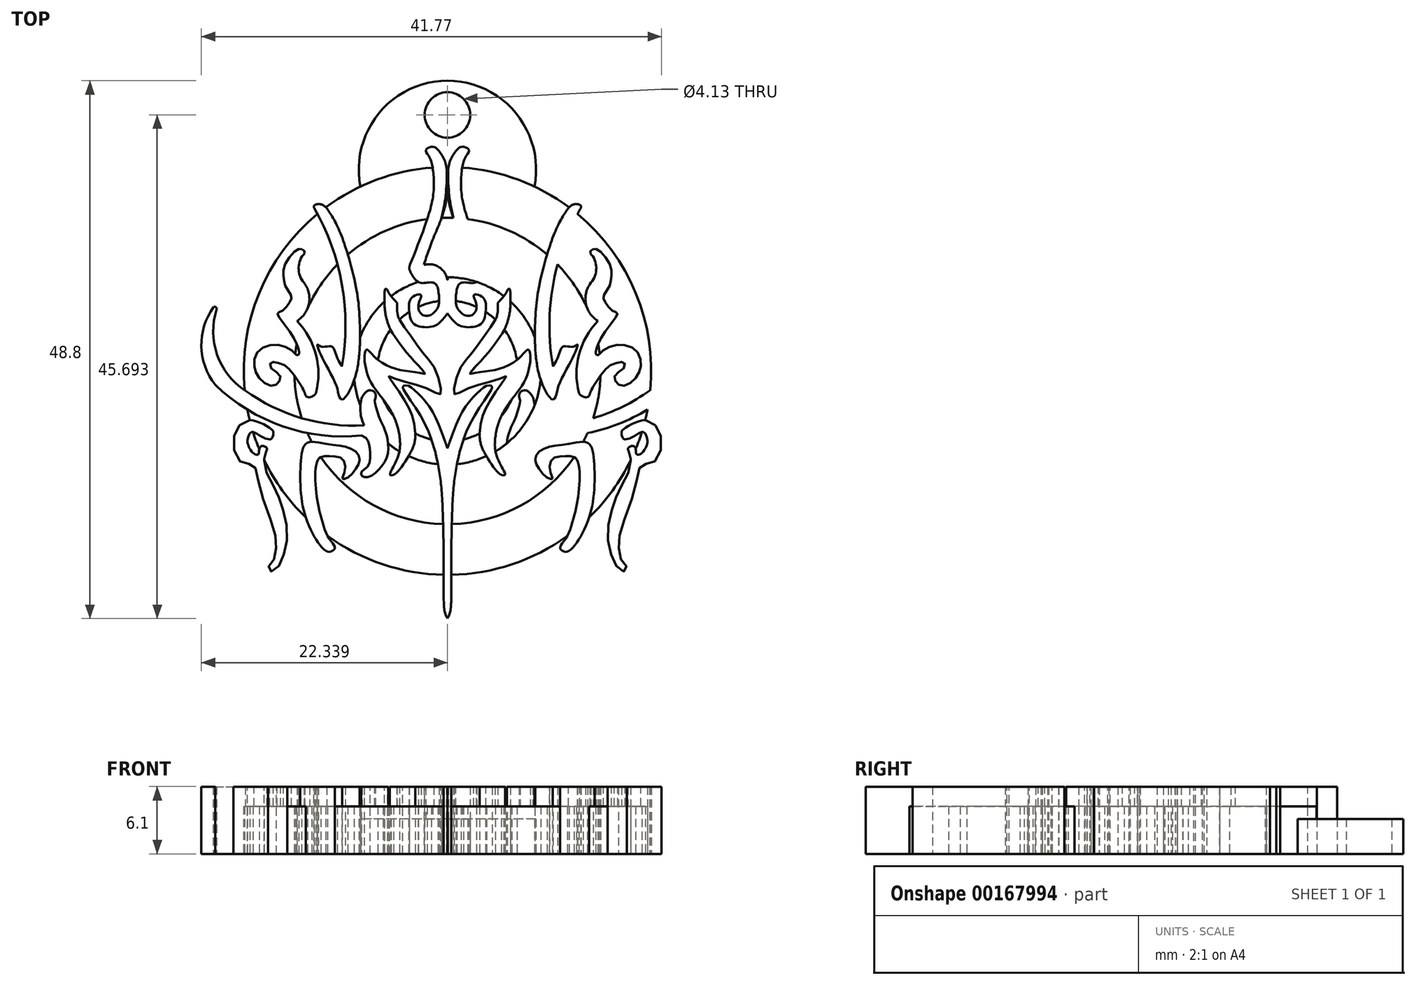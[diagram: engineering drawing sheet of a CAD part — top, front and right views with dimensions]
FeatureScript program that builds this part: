
annotation { "Feature Type Name" : "Feature", "Feature Type Description" : "" }
export const myFeature = defineFeature(function(context is Context, id is Id, definition is map)
    precondition{}
    {
        {
            var Q0;
            Q0=qCreatedBy(makeId("Top.planeOp"),FACE);
            var sketch = newSketch(context, id + "F0", { "sketchPlane" : qUnion([Q0])});
            skFitSpline(sketch, "E0", {"points": [v(-0.36, 46.17) * mm, v(-0.6, 47.55) * mm, v(-1.23, 48.6) * mm, v(-1.62, 48.85) * mm, v(-2.1, 48.77) * mm, v(-2.32, 48.53) * mm, v(-2.06, 48.04) * mm, v(-1.74, 47.2) * mm, v(-1.6, 45.2) * mm, v(-2.2, 42.32) * mm, v(-3.77, 38.15) * mm, v(-3.8, 37.74) * mm, v(-3.02, 36.6) * mm, v(-2.13, 36.55) * mm, v(-1.45, 36.42) * mm, v(-1.17, 35.66) * mm, v(-1.17, 34.49) * mm, v(-1.6, 33.8) * mm, v(-2.13, 33.53) * mm, v(-2.72, 33.68) * mm, v(-3, 34.46) * mm, v(-2.77, 35.23) * mm, v(-2.8, 35.44) * mm, v(-3.57, 35.2) * mm, v(-3.85, 34.31) * mm, v(-3.64, 33.08) * mm, v(-3.09, 32.61) * mm, v(-2.07, 32.5) * mm, v(-1.21, 32.8) * mm, v(-0.36, 33.76) * mm], "startDerivative": vector(-2.43, 33.8) * mm, "endDerivative": vector(19.13, 26.66) * mm});
            skFitSpline(sketch, "E1", {"points": [v(-5.8, 35.84) * mm, v(-5.55, 35.4) * mm, v(-4.93, 34.7) * mm], "startDerivative": vector(0.49, -1.03) * mm, "endDerivative": vector(1.22, -1.28) * mm});
            skFitSpline(sketch, "E2", {"points": [v(-4.93, 34.7) * mm, v(-4.93, 34.14) * mm, v(-4.8, 33.35) * mm, v(-3.77, 31.8) * mm, v(-2.5, 30.04) * mm, v(-1.41, 28.52) * mm, v(-0.96, 26.51) * mm, v(-1.06, 26.41) * mm, v(-2.38, 27) * mm, v(-4.76, 27.69) * mm, v(-5.7, 28.02) * mm, v(-5.58, 27.82) * mm, v(-4.93, 26.92) * mm, v(-3.9, 25.26) * mm, v(-3.45, 24) * mm, v(-3.34, 22.1) * mm, v(-4.21, 20.3) * mm, v(-5.14, 19.16) * mm, v(-5.57, 19.1) * mm, v(-5.44, 19.54) * mm, v(-4.93, 20.51) * mm, v(-4.67, 21.65) * mm, v(-4.93, 23.59) * mm, v(-5.92, 25.58) * mm, v(-7.26, 27.41) * mm, v(-7.83, 29.07) * mm, v(-7.86, 30.2) * mm, v(-7.68, 30.46) * mm, v(-7.41, 30.27) * mm, v(-6.76, 29.59) * mm, v(-5.54, 28.88) * mm, v(-4.11, 28.52) * mm, v(-2.73, 28.32) * mm, v(-2.41, 28.26) * mm, v(-2.68, 28.66) * mm, v(-3.96, 30.06) * mm, v(-4.93, 31.35) * mm, v(-5.5, 32.22) * mm, v(-5.98, 33.65) * mm, v(-6.08, 35.05) * mm, v(-5.98, 35.98) * mm, v(-5.8, 35.84) * mm], "startDerivative": vector(-0.34, -32.03) * mm, "endDerivative": vector(17.35, -24.3) * mm});
            skFitSpline(sketch, "E3", {"points": [v(-0.36, 6.06) * mm, v(-0.6, 6.68) * mm, v(-0.7, 9.02) * mm, v(-0.82, 16.57) * mm, v(-1.2, 19.94) * mm, v(-2.54, 23.98) * mm, v(-4.4, 26.99) * mm, v(-4.35, 27.17) * mm, v(-3.98, 27.2) * mm, v(-3.18, 26.63) * mm, v(-1.8, 24.94) * mm, v(-0.65, 22.32) * mm, v(-0.36, 21.5) * mm], "startDerivative": vector(-5.82, 11.46) * mm, "endDerivative": vector(4.22, -12.55) * mm});
            skLineSegment(sketch, "E4", {"start": v(-0.36, 46.17) * mm, "end": v(-0.36, 46.17) * mm});
            skFitSpline(sketch, "E5", {"points": [v(-2.5, 38.16) * mm, v(-1.58, 38.16) * mm, v(-0.68, 37.53) * mm, v(-0.36, 36.78) * mm], "startDerivative": vector(2.77, 0.4) * mm, "endDerivative": vector(0.67, -2.46) * mm});
            skArc(sketch, "E6", {"start": v(-9.94, 28.94) * mm, "mid": v(-9.94, 36.35) * mm, "end": v(-12.47, 43.31) * mm});
            skFitSpline(sketch, "E7", {"points": [v(-12.47, 43.31) * mm, v(-12.47, 43.53) * mm, v(-11.92, 43.67) * mm, v(-11.33, 43.31) * mm], "startDerivative": vector(-0.3, 1) * mm, "endDerivative": vector(1.33, -1.17) * mm});
            skFitSpline(sketch, "E8", {"points": [v(-11.33, 43.31) * mm, v(-10.2, 41.31) * mm, v(-8.7, 36.35) * mm, v(-8.33, 32.98) * mm, v(-8.7, 28.1) * mm, v(-9.9, 25.95) * mm, v(-10.17, 26.15) * mm, v(-10.43, 27.14) * mm, v(-11.67, 29.6) * mm, v(-12.15, 30.73) * mm], "startDerivative": vector(10.19, -15.18) * mm, "endDerivative": vector(-4.43, 12.34) * mm});
            skFitSpline(sketch, "E9", {"points": [v(-12.15, 30.73) * mm, v(-12.15, 30.92) * mm, v(-11.84, 30.73) * mm, v(-10.86, 30.73) * mm, v(-10.49, 30.02) * mm, v(-9.94, 28.94) * mm], "startDerivative": vector(-0.34, 2.51) * mm, "endDerivative": vector(2.32, -3.87) * mm});
            skArc(sketch, "E10", {"start": v(-13.32, 39.21) * mm, "mid": v(-13.87, 37.88) * mm, "end": v(-13.39, 36.53) * mm});
            skArc(sketch, "E11", {"start": v(-14.03, 33.06) * mm, "mid": v(-12.92, 34.65) * mm, "end": v(-13.39, 36.53) * mm});
            skArc(sketch, "E12", {"start": v(-12.3, 26.5) * mm, "mid": v(-12.3, 30.01) * mm, "end": v(-14.03, 33.06) * mm});
            skFitSpline(sketch, "E13", {"points": [v(-12.3, 26.5) * mm, v(-12.63, 26.2) * mm, v(-13.12, 26.17) * mm, v(-13.36, 26.62) * mm, v(-14.5, 28.46) * mm, v(-15.23, 29.07) * mm, v(-16.06, 29.33) * mm, v(-16.42, 29.26) * mm, v(-16.42, 28.83) * mm, v(-15.64, 28.23) * mm, v(-15.55, 27.76) * mm, v(-15.94, 27.25) * mm, v(-16.7, 27.29) * mm, v(-17.61, 28.1) * mm, v(-17.9, 29) * mm, v(-17.7, 30.12) * mm, v(-16.63, 30.84) * mm, v(-15.17, 30.74) * mm, v(-14.29, 30.2) * mm, v(-14.08, 29.98) * mm, v(-13.85, 30.04) * mm, v(-13.93, 30.63) * mm, v(-14.63, 32.05) * mm, v(-15.8, 33.66) * mm, v(-15.76, 33.82) * mm, v(-15.21, 34.08) * mm, v(-14.61, 34.92) * mm, v(-14.53, 35.34) * mm, v(-15.03, 36.16) * mm, v(-15.23, 37.03) * mm, v(-15.11, 38.16) * mm, v(-14, 39.52) * mm, v(-13.6, 39.58) * mm, v(-13.36, 39.42) * mm, v(-13.32, 39.21) * mm], "startDerivative": vector(-12.43, -15.12) * mm, "endDerivative": vector(-0.18, -14.31) * mm});
            skArc(sketch, "E14", {"start": v(-21.59, 34.32) * mm, "mid": v(-22.7, 30.77) * mm, "end": v(-21.44, 27.27) * mm});
            skArc(sketch, "E15", {"start": v(-21.44, 27.27) * mm, "mid": v(-15.31, 23.5) * mm, "end": v(-8.16, 22.66) * mm});
            skArc(sketch, "E16", {"start": v(-21.3, 34.14) * mm, "mid": v(-21.4, 34.31) * mm, "end": v(-21.59, 34.32) * mm});
            skArc(sketch, "E17", {"start": v(-21.3, 34.14) * mm, "mid": v(-21.27, 30) * mm, "end": v(-18.72, 26.75) * mm});
            skArc(sketch, "E18", {"start": v(-18.72, 26.75) * mm, "mid": v(-13.59, 24.24) * mm, "end": v(-7.91, 23.58) * mm});
            skArc(sketch, "E19", {"start": v(-8.12, 26.15) * mm, "mid": v(-8.27, 24.85) * mm, "end": v(-7.91, 23.58) * mm});
            skFitSpline(sketch, "E20", {"points": [v(-8.12, 26.15) * mm, v(-7.77, 26.6) * mm, v(-7.34, 26.77) * mm, v(-6.94, 26.55) * mm, v(-6.88, 26.15) * mm, v(-6.96, 25.77) * mm, v(-6.45, 24.08) * mm, v(-6, 23.07) * mm, v(-5.75, 21.97) * mm, v(-5.85, 20.7) * mm, v(-6.4, 19.81) * mm, v(-7.38, 18.96) * mm, v(-7.97, 18.92) * mm, v(-8.19, 19.12) * mm, v(-8.12, 19.43) * mm, v(-7.57, 19.93) * mm, v(-7.37, 21.18) * mm, v(-7.52, 22.02) * mm, v(-8.16, 22.66) * mm], "startDerivative": vector(6.68, 10.52) * mm, "endDerivative": vector(-21.28, 6.18) * mm});
            skFitSpline(sketch, "E21", {"points": [v(-16.63, 10.72) * mm, v(-16.2, 11.28) * mm, v(-15.9, 12.49) * mm, v(-16.14, 14.2) * mm, v(-17.43, 18.06) * mm, v(-17.86, 19.8) * mm, v(-18.4, 20.1) * mm, v(-19.17, 20.3) * mm, v(-19.8, 21.82) * mm, v(-19.39, 23.4) * mm, v(-18.32, 24.07) * mm, v(-16.41, 23.3) * mm, v(-16.17, 22.95) * mm, v(-16.3, 22.4) * mm, v(-16.63, 22.33) * mm, v(-17.48, 22.7) * mm, v(-18.16, 22.97) * mm, v(-18.5, 22.36) * mm, v(-18.4, 21.66) * mm, v(-17.94, 21.02) * mm, v(-17.54, 20.96) * mm, v(-17.4, 21.58) * mm, v(-17.08, 21.71) * mm, v(-16.76, 21.52) * mm, v(-16.92, 20.9) * mm, v(-16.84, 19.46) * mm, v(-15.98, 17.74) * mm, v(-15.4, 16.21) * mm, v(-14.91, 13.99) * mm, v(-15.2, 11.9) * mm, v(-15.88, 10.6) * mm, v(-16.5, 10.34) * mm, v(-16.63, 10.72) * mm]});
            skFitSpline(sketch, "E22", {"points": [v(-13.09, 22) * mm, v(-13.68, 20.21) * mm, v(-13.44, 16) * mm, v(-12.26, 13.18) * mm, v(-11.29, 12.14) * mm, v(-10.78, 12.22) * mm, v(-10.6, 12.54) * mm, v(-11.13, 13.37) * mm, v(-11.9, 15.54) * mm, v(-12.34, 18.1) * mm, v(-12.15, 20.43) * mm, v(-11.67, 20.77) * mm, v(-10.91, 20.77) * mm, v(-9.87, 20.53) * mm, v(-9.7, 19.38) * mm, v(-9.9, 18.74) * mm, v(-9.33, 18.9) * mm, v(-8.55, 19.84) * mm, v(-8.34, 20.61) * mm, v(-8.74, 21.26) * mm, v(-9.87, 21.71) * mm, v(-11.4, 21.9) * mm, v(-13.09, 22) * mm]});
            skFitSpline(sketch, "E23.MirrorCS", {"points": [v(-0.36, 6.06) * mm, v(-0.12, 6.68) * mm, v(-0.02, 9.02) * mm, v(0.1, 16.57) * mm, v(0.48, 19.94) * mm, v(1.82, 23.98) * mm, v(3.68, 26.99) * mm, v(3.63, 27.17) * mm, v(3.26, 27.2) * mm, v(2.46, 26.63) * mm, v(1.07, 24.94) * mm, v(-0.08, 22.32) * mm, v(-0.36, 21.5) * mm], "startDerivative": vector(5.82, 11.46) * mm, "endDerivative": vector(-4.22, -12.55) * mm});
            skFitSpline(sketch, "E24.MirrorCS", {"points": [v(1.78, 38.16) * mm, v(0.86, 38.16) * mm, v(-0.05, 37.53) * mm, v(-0.36, 36.78) * mm], "startDerivative": vector(-2.77, 0.4) * mm, "endDerivative": vector(-0.67, -2.46) * mm});
            skFitSpline(sketch, "E25.MirrorCS", {"points": [v(-0.36, 46.17) * mm, v(-0.13, 47.55) * mm, v(0.51, 48.6) * mm, v(0.9, 48.85) * mm, v(1.38, 48.77) * mm, v(1.6, 48.53) * mm, v(1.34, 48.04) * mm, v(1.02, 47.2) * mm, v(0.87, 45.2) * mm, v(1.47, 42.32) * mm, v(3.04, 38.15) * mm, v(3.09, 37.74) * mm, v(2.3, 36.6) * mm, v(1.4, 36.55) * mm, v(0.72, 36.42) * mm, v(0.45, 35.66) * mm, v(0.45, 34.49) * mm, v(0.87, 33.8) * mm, v(1.4, 33.53) * mm, v(2, 33.68) * mm, v(2.28, 34.46) * mm, v(2.04, 35.23) * mm, v(2.09, 35.44) * mm, v(2.85, 35.2) * mm, v(3.13, 34.31) * mm, v(2.92, 33.08) * mm, v(2.37, 32.61) * mm, v(1.35, 32.5) * mm, v(0.5, 32.8) * mm, v(-0.36, 33.76) * mm], "startDerivative": vector(2.43, 33.8) * mm, "endDerivative": vector(-19.13, 26.66) * mm});
            skFitSpline(sketch, "E26.MirrorCS", {"points": [v(5.08, 35.84) * mm, v(4.83, 35.4) * mm, v(4.21, 34.7) * mm], "startDerivative": vector(-0.49, -1.03) * mm, "endDerivative": vector(-1.22, -1.28) * mm});
            skArc(sketch, "E27.MirrorCS", {"start": v(20.58, 34.14) * mm, "mid": v(20.67, 34.31) * mm, "end": v(20.87, 34.32) * mm});
            skFitSpline(sketch, "E28.MirrorCS", {"points": [v(11.75, 43.31) * mm, v(11.75, 43.53) * mm, v(11.2, 43.67) * mm, v(10.6, 43.31) * mm], "startDerivative": vector(0.3, 1) * mm, "endDerivative": vector(-1.33, -1.17) * mm});
            skFitSpline(sketch, "E29.MirrorCS", {"points": [v(11.43, 30.73) * mm, v(11.43, 30.92) * mm, v(11.12, 30.73) * mm, v(10.14, 30.73) * mm, v(9.77, 30.02) * mm, v(9.22, 28.94) * mm], "startDerivative": vector(0.34, 2.51) * mm, "endDerivative": vector(-2.32, -3.87) * mm});
            skFitSpline(sketch, "E30.MirrorCS", {"points": [v(7.4, 26.15) * mm, v(7.05, 26.6) * mm, v(6.62, 26.77) * mm, v(6.21, 26.55) * mm, v(6.16, 26.15) * mm, v(6.23, 25.77) * mm, v(5.72, 24.08) * mm, v(5.28, 23.07) * mm, v(5.03, 21.97) * mm, v(5.13, 20.7) * mm, v(5.67, 19.81) * mm, v(6.66, 18.96) * mm, v(7.25, 18.92) * mm, v(7.47, 19.12) * mm, v(7.4, 19.43) * mm, v(6.84, 19.93) * mm, v(6.65, 21.18) * mm, v(6.8, 22.02) * mm, v(7.44, 22.66) * mm], "startDerivative": vector(-6.68, 10.52) * mm, "endDerivative": vector(21.28, 6.18) * mm});
            skArc(sketch, "E31.MirrorCS", {"start": v(7.4, 26.15) * mm, "mid": v(7.55, 24.85) * mm, "end": v(7.2, 23.58) * mm});
            skFitSpline(sketch, "E32.MirrorCS", {"points": [v(4.21, 34.7) * mm, v(4.21, 34.14) * mm, v(4.07, 33.35) * mm, v(3.05, 31.8) * mm, v(1.77, 30.04) * mm, v(0.7, 28.52) * mm, v(0.24, 26.51) * mm, v(0.34, 26.41) * mm, v(1.65, 27) * mm, v(4.03, 27.69) * mm, v(4.98, 28.02) * mm, v(4.86, 27.82) * mm, v(4.21, 26.92) * mm, v(3.19, 25.26) * mm, v(2.73, 24) * mm, v(2.62, 22.1) * mm, v(3.5, 20.3) * mm, v(4.41, 19.16) * mm, v(4.84, 19.1) * mm, v(4.72, 19.54) * mm, v(4.21, 20.51) * mm, v(3.95, 21.65) * mm, v(4.21, 23.59) * mm, v(5.2, 25.58) * mm, v(6.54, 27.41) * mm, v(7.1, 29.07) * mm, v(7.14, 30.2) * mm, v(6.96, 30.46) * mm, v(6.7, 30.27) * mm, v(6.03, 29.59) * mm, v(4.82, 28.88) * mm, v(3.39, 28.52) * mm, v(2, 28.32) * mm, v(1.7, 28.26) * mm, v(1.96, 28.66) * mm, v(3.24, 30.06) * mm, v(4.21, 31.35) * mm, v(4.78, 32.22) * mm, v(5.26, 33.65) * mm, v(5.36, 35.05) * mm, v(5.26, 35.98) * mm, v(5.08, 35.84) * mm], "startDerivative": vector(0.34, -32.03) * mm, "endDerivative": vector(-17.35, -24.3) * mm});
            skFitSpline(sketch, "E33.MirrorCS", {"points": [v(11.58, 26.5) * mm, v(11.91, 26.2) * mm, v(12.4, 26.17) * mm, v(12.64, 26.62) * mm, v(13.79, 28.46) * mm, v(14.5, 29.07) * mm, v(15.34, 29.33) * mm, v(15.7, 29.26) * mm, v(15.7, 28.83) * mm, v(14.92, 28.23) * mm, v(14.82, 27.76) * mm, v(15.21, 27.25) * mm, v(15.97, 27.29) * mm, v(16.89, 28.1) * mm, v(17.18, 29) * mm, v(16.98, 30.12) * mm, v(15.9, 30.84) * mm, v(14.45, 30.74) * mm, v(13.56, 30.2) * mm, v(13.36, 29.98) * mm, v(13.13, 30.04) * mm, v(13.2, 30.63) * mm, v(13.9, 32.05) * mm, v(15.07, 33.66) * mm, v(15.04, 33.82) * mm, v(14.49, 34.08) * mm, v(13.9, 34.92) * mm, v(13.81, 35.34) * mm, v(14.3, 36.16) * mm, v(14.5, 37.03) * mm, v(14.4, 38.16) * mm, v(13.28, 39.52) * mm, v(12.88, 39.58) * mm, v(12.64, 39.42) * mm, v(12.6, 39.21) * mm], "startDerivative": vector(12.43, -15.12) * mm, "endDerivative": vector(0.18, -14.31) * mm});
            skArc(sketch, "E34.MirrorCS", {"start": v(20.58, 34.14) * mm, "mid": v(20.55, 30) * mm, "end": v(18, 26.75) * mm});
            skFitSpline(sketch, "E35.MirrorC", {"points": [v(15.9, 10.72) * mm, v(15.48, 11.28) * mm, v(15.18, 12.49) * mm, v(15.42, 14.2) * mm, v(16.7, 18.06) * mm, v(17.14, 19.8) * mm, v(17.68, 20.1) * mm, v(18.45, 20.3) * mm, v(19.07, 21.82) * mm, v(18.67, 23.4) * mm, v(17.6, 24.07) * mm, v(15.7, 23.3) * mm, v(15.45, 22.95) * mm, v(15.58, 22.4) * mm, v(15.9, 22.33) * mm, v(16.76, 22.7) * mm, v(17.43, 22.97) * mm, v(17.78, 22.36) * mm, v(17.68, 21.66) * mm, v(17.22, 21.02) * mm, v(16.82, 20.96) * mm, v(16.68, 21.58) * mm, v(16.36, 21.71) * mm, v(16.04, 21.52) * mm, v(16.2, 20.9) * mm, v(16.12, 19.46) * mm, v(15.26, 17.74) * mm, v(14.67, 16.21) * mm, v(14.19, 13.99) * mm, v(14.48, 11.9) * mm, v(15.15, 10.6) * mm, v(15.77, 10.34) * mm, v(15.9, 10.72) * mm]});
            skArc(sketch, "E36.MirrorCS", {"start": v(20.72, 27.27) * mm, "mid": v(14.59, 23.5) * mm, "end": v(7.44, 22.66) * mm});
            skFitSpline(sketch, "E37.MirrorC", {"points": [v(12.36, 22) * mm, v(12.95, 20.21) * mm, v(12.71, 16) * mm, v(11.53, 13.18) * mm, v(10.57, 12.14) * mm, v(10.06, 12.22) * mm, v(9.87, 12.54) * mm, v(10.4, 13.37) * mm, v(11.18, 15.54) * mm, v(11.61, 18.1) * mm, v(11.43, 20.43) * mm, v(10.94, 20.77) * mm, v(10.2, 20.77) * mm, v(9.15, 20.53) * mm, v(8.99, 19.38) * mm, v(9.17, 18.74) * mm, v(8.61, 18.9) * mm, v(7.83, 19.84) * mm, v(7.62, 20.61) * mm, v(8.02, 21.26) * mm, v(9.15, 21.71) * mm, v(10.68, 21.9) * mm, v(12.36, 22) * mm]});
            skArc(sketch, "E38.MirrorCS", {"start": v(13.3, 33.06) * mm, "mid": v(12.2, 34.65) * mm, "end": v(12.67, 36.53) * mm});
            skArc(sketch, "E39.MirrorCS", {"start": v(12.6, 39.21) * mm, "mid": v(13.15, 37.88) * mm, "end": v(12.67, 36.53) * mm});
            skFitSpline(sketch, "E40.MirrorCS", {"points": [v(10.6, 43.31) * mm, v(9.48, 41.31) * mm, v(7.98, 36.35) * mm, v(7.6, 32.98) * mm, v(7.98, 28.1) * mm, v(9.17, 25.95) * mm, v(9.45, 26.15) * mm, v(9.7, 27.14) * mm, v(10.95, 29.6) * mm, v(11.43, 30.73) * mm], "startDerivative": vector(-10.19, -15.18) * mm, "endDerivative": vector(4.43, 12.34) * mm});
            skArc(sketch, "E41.MirrorCS", {"start": v(9.22, 28.94) * mm, "mid": v(9.22, 36.35) * mm, "end": v(11.75, 43.31) * mm});
            skArc(sketch, "E42.MirrorCS", {"start": v(20.87, 34.32) * mm, "mid": v(21.98, 30.77) * mm, "end": v(20.72, 27.27) * mm});
            skArc(sketch, "E43.MirrorCS", {"start": v(11.58, 26.5) * mm, "mid": v(11.57, 30.01) * mm, "end": v(13.3, 33.06) * mm});
            skArc(sketch, "E44.MirrorCS", {"start": v(18, 26.75) * mm, "mid": v(12.87, 24.24) * mm, "end": v(7.2, 23.58) * mm});
            skArc(sketch, "E45", {"start": v(-12.17, 42.77) * mm, "mid": v(-17.45, 35.6) * mm, "end": v(-18.78, 26.78) * mm});
            skArc(sketch, "E46", {"start": v(-10.35, 38.2) * mm, "mid": v(-12.32, 35.6) * mm, "end": v(-13.64, 32.64) * mm});
            skArc(sketch, "E47.trimOffspring", {"start": v(10.68, 43.37) * mm, "mid": v(6.09, 45.86) * mm, "end": v(0.98, 46.98) * mm});
            skArc(sketch, "E48.trimOffspring", {"start": v(8.69, 39.08) * mm, "mid": v(5.31, 41.22) * mm, "end": v(1.47, 42.3) * mm});
            skArc(sketch, "E49.trimOffspring", {"start": v(-2.2, 42.3) * mm, "mid": v(-6.04, 41.22) * mm, "end": v(-9.4, 39.08) * mm});
            skArc(sketch, "E50.trimOffspring", {"start": v(0.18, 42.42) * mm, "mid": v(-0.36, 42.43) * mm, "end": v(-0.9, 42.42) * mm});
            skArc(sketch, "E51.trimOffspring", {"start": v(-1.7, 46.98) * mm, "mid": v(-6.8, 45.86) * mm, "end": v(-11.4, 43.37) * mm});
            skArc(sketch, "E52.trimOffspring", {"start": v(-0.27, 47.02) * mm, "mid": v(-0.36, 47.02) * mm, "end": v(-0.45, 47.02) * mm});
            skArc(sketch, "E53.trimOffspring", {"start": v(0.03, 14.63) * mm, "mid": v(6.32, 16.33) * mm, "end": v(11.14, 20.71) * mm});
            skArc(sketch, "E54.trimOffspring", {"start": v(-0.02, 10.03) * mm, "mid": v(5.52, 10.99) * mm, "end": v(10.52, 13.56) * mm});
            skArc(sketch, "E55.trimOffspring", {"start": v(-11.24, 13.56) * mm, "mid": v(-6.24, 10.99) * mm, "end": v(-0.7, 10.03) * mm});
            skArc(sketch, "E56.trimOffspring", {"start": v(-11.86, 20.71) * mm, "mid": v(-7.04, 16.33) * mm, "end": v(-0.75, 14.63) * mm});
            skArc(sketch, "E57.trimOffspring", {"start": v(11.97, 22.1) * mm, "mid": v(12.17, 22.5) * mm, "end": v(12.35, 22.9) * mm});
            skArc(sketch, "E58.trimOffspring", {"start": v(12.5, 15.23) * mm, "mid": v(14.61, 17.66) * mm, "end": v(16.27, 20.42) * mm});
            skArc(sketch, "E59.trimOffspring", {"start": v(-18, 22.98) * mm, "mid": v(-17.74, 22.2) * mm, "end": v(-17.44, 21.43) * mm});
            skArc(sketch, "E60.trimOffspring", {"start": v(-17, 20.42) * mm, "mid": v(-15.33, 17.66) * mm, "end": v(-13.22, 15.23) * mm});
            skArc(sketch, "E61.trimOffspring", {"start": v(16.72, 21.43) * mm, "mid": v(17.02, 22.2) * mm, "end": v(17.29, 22.98) * mm});
            skArc(sketch, "E62.trimOffspring", {"start": v(-14.05, 30.97) * mm, "mid": v(-14.12, 30.52) * mm, "end": v(-14.18, 30.06) * mm});
            skArc(sketch, "E63.trimOffspring", {"start": v(-14.26, 28.13) * mm, "mid": v(-14.06, 26.16) * mm, "end": v(-13.59, 24.24) * mm});
            skArc(sketch, "E64.trimOffspring", {"start": v(-13.07, 22.9) * mm, "mid": v(-12.89, 22.5) * mm, "end": v(-12.7, 22.1) * mm});
            skArc(sketch, "E65.trimOffspring", {"start": v(-18.52, 25.01) * mm, "mid": v(-18.43, 24.54) * mm, "end": v(-18.32, 24.07) * mm});
            skArc(sketch, "E66.trimOffspring", {"start": v(17.6, 24.07) * mm, "mid": v(17.7, 24.54) * mm, "end": v(17.8, 25.01) * mm});
            skArc(sketch, "E67.trimOffspring", {"start": v(18.06, 26.78) * mm, "mid": v(16.73, 35.6) * mm, "end": v(11.44, 42.77) * mm});
            skArc(sketch, "E68.trimOffspring", {"start": v(12.87, 24.24) * mm, "mid": v(13.34, 26.16) * mm, "end": v(13.54, 28.13) * mm});
            skArc(sketch, "E69.trimOffspring", {"start": v(13.46, 30.06) * mm, "mid": v(13.4, 30.52) * mm, "end": v(13.33, 30.97) * mm});
            skArc(sketch, "E70.trimOffspring", {"start": v(12.92, 32.64) * mm, "mid": v(11.6, 35.6) * mm, "end": v(9.63, 38.2) * mm});
            skFitSpline(sketch, "E71.trimOffspring", {"points": [v(-0.36, 46.17) * mm, v(-0.6, 43.37) * mm, v(-1.74, 40.32) * mm, v(-2.5, 38.16) * mm], "startDerivative": vector(-0.07, -8.23) * mm, "endDerivative": vector(-2.19, -6.82) * mm});
            skFitSpline(sketch, "E72.trimOffspring", {"points": [v(-0.36, 46.17) * mm, v(-0.11, 43.37) * mm, v(1.02, 40.32) * mm, v(1.78, 38.16) * mm], "startDerivative": vector(0.07, -8.23) * mm, "endDerivative": vector(2.19, -6.82) * mm});
            skArc(sketch, "E73", {"start": v(-0.9, 42.42) * mm, "mid": v(-0.5, 44.7) * mm, "end": v(-0.45, 47.02) * mm});
            skArc(sketch, "E74.MirrorCS", {"start": v(0.18, 42.42) * mm, "mid": v(-0.22, 44.7) * mm, "end": v(-0.27, 47.02) * mm});
            skCircle(sketch, "E75", {"center": v(-0.36, 28.52) * mm, "radius": 8.5 * mm});
            skCircle(sketch, "E76", {"center": v(-0.36, 28.52) * mm, "radius": 6.38 * mm});
            skLineSegment(sketch, "E77", {"start": v(-0.36, 46.17) * mm, "end": v(-0.36, 50.4) * mm});
            skCircle(sketch, "E78", {"center": v(-0.36, 51.75) * mm, "radius": 2.06 * mm});
            skArc(sketch, "E79", {"start": v(7.53, 45.26) * mm, "mid": v(-0.36, 54.86) * mm, "end": v(-8.25, 45.26) * mm});
            skSolve(sketch);
        }
        {
            var Q0;
            {var subQ5=sQuery(id+"F0.wireOp",EDGE,"E9");Q0=makeQuery(id+"F0.imprint","IMPRINT",FACE,{"disambiguationData":[TD([[makeQuery(id+"F0.imprint","IMPRINT",EDGE,{"derivedFrom":subQ5}),-1.0]])]});}
            var Q1;
            {var subQ6=sQuery(id+"F0.wireOp",EDGE,"E10");Q1=makeQuery(id+"F0.imprint","IMPRINT",FACE,{"disambiguationData":[TD([[makeQuery(id+"F0.imprint","IMPRINT",EDGE,{"derivedFrom":subQ6}),-1.0]])]});}
            var Q2;
            {var subQ4=sQuery(id+"F0.wireOp",EDGE,"E14");Q2=makeQuery(id+"F0.imprint","IMPRINT",FACE,{"disambiguationData":[TD([[makeQuery(id+"F0.imprint","IMPRINT",EDGE,{"derivedFrom":subQ4}),1.0]])]});}
            var Q3;
            {var subQ0=sQuery(id+"F0.wireOp",EDGE,"E59.trimOffspring");var subQ1=sQuery(id+"F0.wireOp",EDGE,"E21");var subQ2=makeQuery(id+"F0.imprint","INTERSECT",VERTEX,{"disambiguationData":[OD(0.0)],"derivedFrom":[subQ1,subQ0]});Q3=makeQuery(id+"F0.imprint","IMPRINT",FACE,{"disambiguationData":[TD([[makeQuery(id+"F0.imprint","IMPRINT",EDGE,{"disambiguationData":[TD([[subQ2,1.0]])],"derivedFrom":subQ1}),-1.0]])]});}
            var Q4;
            {var subQ0=sQuery(id+"F0.wireOp",EDGE,"E22");var subQ1=makeQuery(id+"F0.imprint","INTERSECT",VERTEX,{"derivedFrom":[subQ0,sQuery(id+"F0.wireOp",EDGE,"E55.trimOffspring")]});Q4=makeQuery(id+"F0.imprint","IMPRINT",FACE,{"disambiguationData":[TD([[makeQuery(id+"F0.imprint","IMPRINT",EDGE,{"disambiguationData":[TD([[subQ1,1.0]])],"derivedFrom":subQ0}),1.0]])]});}
            var Q5;
            {var subQ0=sQuery(id+"F0.wireOp",EDGE,"E61.trimOffspring");var subQ1=sQuery(id+"F0.wireOp",EDGE,"E35.MirrorC");var subQ2=makeQuery(id+"F0.imprint","INTERSECT",VERTEX,{"disambiguationData":[OD(1.0)],"derivedFrom":[subQ1,subQ0]});Q5=makeQuery(id+"F0.imprint","IMPRINT",FACE,{"disambiguationData":[TD([[makeQuery(id+"F0.imprint","IMPRINT",EDGE,{"disambiguationData":[TD([[subQ2,1.0]])],"derivedFrom":subQ1}),1.0]])]});}
            var Q6;
            {var subQ0=sQuery(id+"F0.wireOp",EDGE,"E37.MirrorC");var subQ1=makeQuery(id+"F0.imprint","INTERSECT",VERTEX,{"derivedFrom":[subQ0,sQuery(id+"F0.wireOp",EDGE,"E54.trimOffspring")]});Q6=makeQuery(id+"F0.imprint","IMPRINT",FACE,{"disambiguationData":[TD([[makeQuery(id+"F0.imprint","IMPRINT",EDGE,{"disambiguationData":[TD([[subQ1,1.0]])],"derivedFrom":subQ0}),-1.0]])]});}
            var Q7;
            {var subQ0=sQuery(id+"F0.wireOp",EDGE,"E23.MirrorCS");var subQ1=sQuery(id+"F0.wireOp",EDGE,"E3");var subQ2=makeQuery(id+"F0.imprint","INTERSECT",VERTEX,{"disambiguationData":[OD(0.0)],"derivedFrom":[subQ1,subQ0]});Q7=makeQuery(id+"F0.imprint","IMPRINT",FACE,{"disambiguationData":[TD([[makeQuery(id+"F0.imprint","IMPRINT",EDGE,{"disambiguationData":[TD([[subQ2,-1.0]])],"derivedFrom":subQ1}),-1.0]])]});}
            var Q8;
            Q8=makeQuery(id+"F0.imprint","IMPRINT",FACE,{"disambiguationData":[TD([[makeQuery(id+"F0.imprint","IMPRINT",EDGE,{"derivedFrom":sQuery(id+"F0.wireOp",EDGE,"E1")}),-1.0]])]});
            var Q9;
            Q9=makeQuery(id+"F0.imprint","IMPRINT",FACE,{"disambiguationData":[TD([[makeQuery(id+"F0.imprint","IMPRINT",EDGE,{"derivedFrom":sQuery(id+"F0.wireOp",EDGE,"E26.MirrorCS")}),1.0]])]});
            var Q10;
            {var subQ9=sQuery(id+"F0.wireOp",EDGE,"E27.MirrorCS");Q10=makeQuery(id+"F0.imprint","IMPRINT",FACE,{"disambiguationData":[TD([[makeQuery(id+"F0.imprint","IMPRINT",EDGE,{"derivedFrom":subQ9}),-1.0]])]});}
            var Q11;
            {var subQ4=sQuery(id+"F0.wireOp",EDGE,"E29.MirrorCS");Q11=makeQuery(id+"F0.imprint","IMPRINT",FACE,{"disambiguationData":[TD([[makeQuery(id+"F0.imprint","IMPRINT",EDGE,{"derivedFrom":subQ4}),1.0]])]});}
            var Q12;
            {var subQ0=sQuery(id+"F0.wireOp",EDGE,"E39.MirrorCS");Q12=makeQuery(id+"F0.imprint","IMPRINT",FACE,{"disambiguationData":[TD([[makeQuery(id+"F0.imprint","IMPRINT",EDGE,{"derivedFrom":subQ0}),1.0]])]});}
            var Q13;
            Q13=makeQuery(id+"F0.imprint","IMPRINT",FACE,{"disambiguationData":[TD([[makeQuery(id+"F0.imprint","IMPRINT",EDGE,{"derivedFrom":sQuery(id+"F0.wireOp",EDGE,"E5")}),-1.0]])]});
            var Q14;
            {var subQ8=sQuery(id+"F0.wireOp",EDGE,"E72.trimOffspring");Q14=makeQuery(id+"F0.imprint","IMPRINT",FACE,{"disambiguationData":[TD([[makeQuery(id+"F0.imprint","IMPRINT",EDGE,{"derivedFrom":subQ8}),1.0]])]});}
            var Q15;
            {var subQ0=sQuery(id+"F0.wireOp",EDGE,"E76");var subQ4=sQuery(id+"F0.wireOp",EDGE,"E0");var subQ9=makeQuery(id+"F0.imprint","INTERSECT",VERTEX,{"disambiguationData":[OD(0.0)],"derivedFrom":[subQ4,subQ0]});Q15=makeQuery(id+"F0.imprint","IMPRINT",FACE,{"disambiguationData":[TD([[makeQuery(id+"F0.imprint","IMPRINT",EDGE,{"disambiguationData":[TD([[subQ9,-1.0]])],"derivedFrom":subQ4}),1.0]])]});}
            var Q16;
            {var subQ0=sQuery(id+"F0.wireOp",EDGE,"E76");var subQ1=sQuery(id+"F0.wireOp",EDGE,"E2");var subQ5=makeQuery(id+"F0.imprint","INTERSECT",VERTEX,{"disambiguationData":[OD(0.0)],"derivedFrom":[subQ1,subQ0]});Q16=makeQuery(id+"F0.imprint","IMPRINT",FACE,{"disambiguationData":[TD([[makeQuery(id+"F0.imprint","IMPRINT",EDGE,{"disambiguationData":[TD([[subQ5,-1.0]])],"derivedFrom":subQ1}),-1.0]])]});}
            var Q17;
            {var subQ1=sQuery(id+"F0.wireOp",EDGE,"E2");var subQ5=sQuery(id+"F0.wireOp",EDGE,"E1");var subQ7=makeQuery(id+"F0.imprint","INTERSECT",VERTEX,{"disambiguationData":[OD(1.0)],"derivedFrom":[subQ5,subQ1]});Q17=makeQuery(id+"F0.imprint","IMPRINT",FACE,{"disambiguationData":[TD([[makeQuery(id+"F0.imprint","IMPRINT",EDGE,{"disambiguationData":[TD([[subQ7,1.0]])],"derivedFrom":subQ5}),-1.0]])]});}
            var Q18;
            {var subQ0=sQuery(id+"F0.wireOp",EDGE,"E76");var subQ1=sQuery(id+"F0.wireOp",EDGE,"E2");var subQ2=makeQuery(id+"F0.imprint","INTERSECT",VERTEX,{"disambiguationData":[OD(3.0)],"derivedFrom":[subQ1,subQ0]});Q18=makeQuery(id+"F0.imprint","IMPRINT",FACE,{"disambiguationData":[TD([[makeQuery(id+"F0.imprint","IMPRINT",EDGE,{"disambiguationData":[TD([[subQ2,-1.0]])],"derivedFrom":subQ1}),-1.0]])]});}
            var Q19;
            {var subQ0=sQuery(id+"F0.wireOp",EDGE,"E20");var subQ1=sQuery(id+"F0.wireOp",EDGE,"E19");var subQ2=makeQuery(id+"F0.imprint","INTERSECT",VERTEX,{"derivedFrom":[subQ1,subQ0]});Q19=makeQuery(id+"F0.imprint","IMPRINT",FACE,{"disambiguationData":[TD([[makeQuery(id+"F0.imprint","IMPRINT",EDGE,{"disambiguationData":[TD([[subQ2,-1.0]])],"derivedFrom":subQ1}),1.0]])]});}
            var Q20;
            {var subQ0=sQuery(id+"F0.wireOp",EDGE,"E76");var subQ1=sQuery(id+"F0.wireOp",EDGE,"E2");var subQ2=makeQuery(id+"F0.imprint","INTERSECT",VERTEX,{"disambiguationData":[OD(1.0)],"derivedFrom":[subQ1,subQ0]});Q20=makeQuery(id+"F0.imprint","IMPRINT",FACE,{"disambiguationData":[TD([[makeQuery(id+"F0.imprint","IMPRINT",EDGE,{"disambiguationData":[TD([[subQ2,-1.0]])],"derivedFrom":subQ1}),-1.0]])]});}
            var Q21;
            {var subQ0=sQuery(id+"F0.wireOp",EDGE,"E76");var subQ1=sQuery(id+"F0.wireOp",EDGE,"E32.MirrorCS");var subQ2=makeQuery(id+"F0.imprint","INTERSECT",VERTEX,{"disambiguationData":[OD(1.0)],"derivedFrom":[subQ1,subQ0]});Q21=makeQuery(id+"F0.imprint","IMPRINT",FACE,{"disambiguationData":[TD([[makeQuery(id+"F0.imprint","IMPRINT",EDGE,{"disambiguationData":[TD([[subQ2,-1.0]])],"derivedFrom":subQ1}),1.0]])]});}
            var Q22;
            {var subQ0=sQuery(id+"F0.wireOp",EDGE,"E76");var subQ1=sQuery(id+"F0.wireOp",EDGE,"E23.MirrorCS");var subQ2=makeQuery(id+"F0.imprint","INTERSECT",VERTEX,{"disambiguationData":[OD(0.0)],"derivedFrom":[subQ1,subQ0]});Q22=makeQuery(id+"F0.imprint","IMPRINT",FACE,{"disambiguationData":[TD([[makeQuery(id+"F0.imprint","IMPRINT",EDGE,{"disambiguationData":[TD([[subQ2,-1.0]])],"derivedFrom":subQ1}),1.0]])]});}
            var Q23;
            {var subQ1=sQuery(id+"F0.wireOp",EDGE,"E3");var subQ7=sQuery(id+"F0.wireOp",EDGE,"E75");var subQ10=makeQuery(id+"F0.imprint","INTERSECT",VERTEX,{"derivedFrom":[subQ1,subQ7]});Q23=makeQuery(id+"F0.imprint","IMPRINT",FACE,{"disambiguationData":[TD([[makeQuery(id+"F0.imprint","IMPRINT",EDGE,{"disambiguationData":[TD([[subQ10,-1.0]])],"derivedFrom":subQ1}),-1.0]])]});}
            var Q24;
            {var subQ0=sQuery(id+"F0.wireOp",EDGE,"E76");var subQ1=sQuery(id+"F0.wireOp",EDGE,"E3");var subQ2=makeQuery(id+"F0.imprint","INTERSECT",VERTEX,{"disambiguationData":[OD(0.0)],"derivedFrom":[subQ1,subQ0]});Q24=makeQuery(id+"F0.imprint","IMPRINT",FACE,{"disambiguationData":[TD([[makeQuery(id+"F0.imprint","IMPRINT",EDGE,{"disambiguationData":[TD([[subQ2,-1.0]])],"derivedFrom":subQ1}),-1.0]])]});}
            var Q25;
            {var subQ0=sQuery(id+"F0.wireOp",EDGE,"E75");var subQ1=sQuery(id+"F0.wireOp",EDGE,"E2");var subQ2=makeQuery(id+"F0.imprint","INTERSECT",VERTEX,{"disambiguationData":[OD(0.0)],"derivedFrom":[subQ1,subQ0]});Q25=makeQuery(id+"F0.imprint","IMPRINT",FACE,{"disambiguationData":[TD([[makeQuery(id+"F0.imprint","IMPRINT",EDGE,{"disambiguationData":[TD([[subQ2,-1.0]])],"derivedFrom":subQ1}),-1.0]])]});}
            var Q26;
            {var subQ0=sQuery(id+"F0.wireOp",EDGE,"E75");var subQ1=sQuery(id+"F0.wireOp",EDGE,"E32.MirrorCS");var subQ2=makeQuery(id+"F0.imprint","INTERSECT",VERTEX,{"disambiguationData":[OD(0.0)],"derivedFrom":[subQ1,subQ0]});Q26=makeQuery(id+"F0.imprint","IMPRINT",FACE,{"disambiguationData":[TD([[makeQuery(id+"F0.imprint","IMPRINT",EDGE,{"disambiguationData":[TD([[subQ2,-1.0]])],"derivedFrom":subQ1}),1.0]])]});}
            var Q27;
            {var subQ0=sQuery(id+"F0.wireOp",EDGE,"E31.MirrorCS");var subQ1=sQuery(id+"F0.wireOp",EDGE,"E30.MirrorCS");var subQ2=makeQuery(id+"F0.imprint","INTERSECT",VERTEX,{"derivedFrom":[subQ1,subQ0]});Q27=makeQuery(id+"F0.imprint","IMPRINT",FACE,{"disambiguationData":[TD([[makeQuery(id+"F0.imprint","IMPRINT",EDGE,{"disambiguationData":[TD([[subQ2,-1.0]])],"derivedFrom":subQ1}),1.0]])]});}
            var Q28;
            {var subQ0=sQuery(id+"F0.wireOp",EDGE,"E76");var subQ1=sQuery(id+"F0.wireOp",EDGE,"E32.MirrorCS");var subQ6=makeQuery(id+"F0.imprint","INTERSECT",VERTEX,{"disambiguationData":[OD(0.0)],"derivedFrom":[subQ1,subQ0]});Q28=makeQuery(id+"F0.imprint","IMPRINT",FACE,{"disambiguationData":[TD([[makeQuery(id+"F0.imprint","IMPRINT",EDGE,{"disambiguationData":[TD([[subQ6,-1.0]])],"derivedFrom":subQ1}),1.0]])]});}
            var Q29;
            {var subQ0=sQuery(id+"F0.wireOp",EDGE,"E76");var subQ1=sQuery(id+"F0.wireOp",EDGE,"E32.MirrorCS");var subQ2=makeQuery(id+"F0.imprint","INTERSECT",VERTEX,{"disambiguationData":[OD(3.0)],"derivedFrom":[subQ1,subQ0]});Q29=makeQuery(id+"F0.imprint","IMPRINT",FACE,{"disambiguationData":[TD([[makeQuery(id+"F0.imprint","IMPRINT",EDGE,{"disambiguationData":[TD([[subQ2,-1.0]])],"derivedFrom":subQ1}),1.0]])]});}
            var Q30;
            {var subQ1=sQuery(id+"F0.wireOp",EDGE,"E26.MirrorCS");var subQ3=sQuery(id+"F0.wireOp",EDGE,"E32.MirrorCS");var subQ5=makeQuery(id+"F0.imprint","INTERSECT",VERTEX,{"disambiguationData":[OD(1.0)],"derivedFrom":[subQ1,subQ3]});Q30=makeQuery(id+"F0.imprint","IMPRINT",FACE,{"disambiguationData":[TD([[makeQuery(id+"F0.imprint","IMPRINT",EDGE,{"disambiguationData":[TD([[subQ5,1.0]])],"derivedFrom":subQ1}),1.0]])]});}
            var Q31;
            {var subQ0=sQuery(id+"F0.wireOp",EDGE,"E76");var subQ1=sQuery(id+"F0.wireOp",EDGE,"E25.MirrorCS");var subQ2=makeQuery(id+"F0.imprint","INTERSECT",VERTEX,{"disambiguationData":[OD(1.0)],"derivedFrom":[subQ1,subQ0]});Q31=makeQuery(id+"F0.imprint","IMPRINT",FACE,{"disambiguationData":[TD([[makeQuery(id+"F0.imprint","IMPRINT",EDGE,{"disambiguationData":[TD([[subQ2,-1.0]])],"derivedFrom":subQ1}),-1.0]])]});}
            var Q32;
            {var subQ0=sQuery(id+"F0.wireOp",EDGE,"E76");var subQ1=sQuery(id+"F0.wireOp",EDGE,"E0");var subQ2=makeQuery(id+"F0.imprint","INTERSECT",VERTEX,{"disambiguationData":[OD(1.0)],"derivedFrom":[subQ1,subQ0]});Q32=makeQuery(id+"F0.imprint","IMPRINT",FACE,{"disambiguationData":[TD([[makeQuery(id+"F0.imprint","IMPRINT",EDGE,{"disambiguationData":[TD([[subQ2,-1.0]])],"derivedFrom":subQ1}),1.0]])]});}
            var Q33;
            {var subQ0=sQuery(id+"F0.wireOp",EDGE,"E75");var subQ1=sQuery(id+"F0.wireOp",EDGE,"E8");var subQ2=makeQuery(id+"F0.imprint","INTERSECT",VERTEX,{"disambiguationData":[OD(0.0)],"derivedFrom":[subQ1,subQ0]});Q33=makeQuery(id+"F0.imprint","IMPRINT",FACE,{"disambiguationData":[TD([[makeQuery(id+"F0.imprint","IMPRINT",EDGE,{"disambiguationData":[TD([[subQ2,-1.0]])],"derivedFrom":subQ1}),-1.0]])]});}
            var Q34;
            {var subQ0=sQuery(id+"F0.wireOp",EDGE,"E75");var subQ1=sQuery(id+"F0.wireOp",EDGE,"E40.MirrorCS");var subQ2=makeQuery(id+"F0.imprint","INTERSECT",VERTEX,{"disambiguationData":[OD(0.0)],"derivedFrom":[subQ1,subQ0]});Q34=makeQuery(id+"F0.imprint","IMPRINT",FACE,{"disambiguationData":[TD([[makeQuery(id+"F0.imprint","IMPRINT",EDGE,{"disambiguationData":[TD([[subQ2,-1.0]])],"derivedFrom":subQ1}),1.0]])]});}
            extrude(context, id + "F1", {"entities" : qUnion([Q0, Q1, Q2, Q3, Q4, Q5, Q6, Q7, Q8, Q9, Q10, Q11, Q12, Q13, Q14, Q15, Q16, Q17, Q18, Q19, Q20, Q21, Q22, Q23, Q24, Q25, Q26, Q27, Q28, Q29, Q30, Q31, Q32, Q33, Q34]), "depth" : 6.1 * mm});
        }
        {
            var Q0;
            {var subQ0=sQuery(id+"F0.wireOp",EDGE,"E49.trimOffspring");Q0=makeQuery(id+"F0.imprint","IMPRINT",FACE,{"disambiguationData":[TD([[makeQuery(id+"F0.imprint","IMPRINT",EDGE,{"derivedFrom":subQ0}),-1.0]])]});}
            var Q1;
            Q1=makeQuery(id+"F0.imprint","IMPRINT",FACE,{"disambiguationData":[TD([[makeQuery(id+"F0.imprint","IMPRINT",EDGE,{"derivedFrom":sQuery(id+"F0.wireOp",EDGE,"E50.trimOffspring")}),-1.0]])]});
            var Q2;
            {var subQ0=sQuery(id+"F0.wireOp",EDGE,"E47.trimOffspring");Q2=makeQuery(id+"F0.imprint","IMPRINT",FACE,{"disambiguationData":[TD([[makeQuery(id+"F0.imprint","IMPRINT",EDGE,{"derivedFrom":subQ0}),1.0]])]});}
            var Q3;
            {var subQ1=sQuery(id+"F0.wireOp",EDGE,"E39.MirrorCS");Q3=makeQuery(id+"F0.imprint","IMPRINT",FACE,{"disambiguationData":[TD([[makeQuery(id+"F0.imprint","IMPRINT",EDGE,{"derivedFrom":subQ1}),-1.0]])]});}
            var Q4;
            {var subQ0=sQuery(id+"F0.wireOp",EDGE,"E57.trimOffspring");Q4=makeQuery(id+"F0.imprint","IMPRINT",FACE,{"disambiguationData":[TD([[makeQuery(id+"F0.imprint","IMPRINT",EDGE,{"derivedFrom":subQ0}),-1.0]])]});}
            var Q5;
            {var subQ0=sQuery(id+"F0.wireOp",EDGE,"E59.trimOffspring");Q5=makeQuery(id+"F0.imprint","IMPRINT",FACE,{"disambiguationData":[TD([[makeQuery(id+"F0.imprint","IMPRINT",EDGE,{"derivedFrom":subQ0}),1.0]])]});}
            var Q6;
            {var subQ0=sQuery(id+"F0.wireOp",EDGE,"E55.trimOffspring");Q6=makeQuery(id+"F0.imprint","IMPRINT",FACE,{"disambiguationData":[TD([[makeQuery(id+"F0.imprint","IMPRINT",EDGE,{"derivedFrom":subQ0}),1.0]])]});}
            var Q7;
            {var subQ0=sQuery(id+"F0.wireOp",EDGE,"E53.trimOffspring");Q7=makeQuery(id+"F0.imprint","IMPRINT",FACE,{"disambiguationData":[TD([[makeQuery(id+"F0.imprint","IMPRINT",EDGE,{"derivedFrom":subQ0}),-1.0]])]});}
            var Q8;
            {var subQ11=sQuery(id+"F0.wireOp",EDGE,"E10");Q8=makeQuery(id+"F0.imprint","IMPRINT",FACE,{"disambiguationData":[TD([[makeQuery(id+"F0.imprint","IMPRINT",EDGE,{"derivedFrom":subQ11}),1.0]])]});}
            var Q9;
            {var subQ0=sQuery(id+"F0.wireOp",EDGE,"E75");var subQ5=sQuery(id+"F0.wireOp",EDGE,"E2");var subQ14=makeQuery(id+"F0.imprint","INTERSECT",VERTEX,{"disambiguationData":[OD(1.0)],"derivedFrom":[subQ5,subQ0]});Q9=makeQuery(id+"F0.imprint","IMPRINT",FACE,{"disambiguationData":[TD([[makeQuery(id+"F0.imprint","IMPRINT",EDGE,{"disambiguationData":[TD([[subQ14,-1.0]])],"derivedFrom":subQ5}),1.0]])]});}
            var Q10;
            {var subQ5=sQuery(id+"F0.wireOp",EDGE,"E75");var subQ7=sQuery(id+"F0.wireOp",EDGE,"E0");var subQ10=makeQuery(id+"F0.imprint","INTERSECT",VERTEX,{"derivedFrom":[subQ7,subQ5]});Q10=makeQuery(id+"F0.imprint","IMPRINT",FACE,{"disambiguationData":[TD([[makeQuery(id+"F0.imprint","IMPRINT",EDGE,{"disambiguationData":[TD([[subQ10,-1.0]])],"derivedFrom":subQ7}),-1.0]])]});}
            var Q11;
            {var subQ3=sQuery(id+"F0.wireOp",EDGE,"E75");var subQ6=sQuery(id+"F0.wireOp",EDGE,"E25.MirrorCS");var subQ10=makeQuery(id+"F0.imprint","INTERSECT",VERTEX,{"derivedFrom":[subQ6,subQ3]});Q11=makeQuery(id+"F0.imprint","IMPRINT",FACE,{"disambiguationData":[TD([[makeQuery(id+"F0.imprint","IMPRINT",EDGE,{"disambiguationData":[TD([[subQ10,-1.0]])],"derivedFrom":subQ6}),1.0]])]});}
            var Q12;
            {var subQ1=sQuery(id+"F0.wireOp",EDGE,"E31.MirrorCS");var subQ11=sQuery(id+"F0.wireOp",EDGE,"E30.MirrorCS");var subQ12=makeQuery(id+"F0.imprint","INTERSECT",VERTEX,{"derivedFrom":[subQ11,subQ1]});Q12=makeQuery(id+"F0.imprint","IMPRINT",FACE,{"disambiguationData":[TD([[makeQuery(id+"F0.imprint","IMPRINT",EDGE,{"disambiguationData":[TD([[subQ12,-1.0]])],"derivedFrom":subQ11}),-1.0]])]});}
            var Q13;
            {var subQ0=sQuery(id+"F0.wireOp",EDGE,"E75");var subQ1=sQuery(id+"F0.wireOp",EDGE,"E23.MirrorCS");var subQ2=makeQuery(id+"F0.imprint","INTERSECT",VERTEX,{"derivedFrom":[subQ1,subQ0]});Q13=makeQuery(id+"F0.imprint","IMPRINT",FACE,{"disambiguationData":[TD([[makeQuery(id+"F0.imprint","IMPRINT",EDGE,{"disambiguationData":[TD([[subQ2,-1.0]])],"derivedFrom":subQ1}),-1.0]])]});}
            var Q14;
            {var subQ0=sQuery(id+"F0.wireOp",EDGE,"E76");var subQ1=sQuery(id+"F0.wireOp",EDGE,"E2");var subQ2=makeQuery(id+"F0.imprint","INTERSECT",VERTEX,{"disambiguationData":[OD(1.0)],"derivedFrom":[subQ1,subQ0]});Q14=makeQuery(id+"F0.imprint","IMPRINT",FACE,{"disambiguationData":[TD([[makeQuery(id+"F0.imprint","IMPRINT",EDGE,{"disambiguationData":[TD([[subQ2,-1.0]])],"derivedFrom":subQ1}),1.0]])]});}
            extrude(context, id + "F2", {"entities" : qUnion([Q0, Q1, Q2, Q3, Q4, Q5, Q6, Q7, Q8, Q9, Q10, Q11, Q12, Q13, Q14]), "operationType" : NewBodyOperationType.ADD, "depth" : 4.32 * mm});
        }
        {
            var Q0;
            Q0=makeQuery(id+"F0.imprint","IMPRINT",FACE,{"disambiguationData":[TD([[makeQuery(id+"F0.imprint","IMPRINT",EDGE,{"derivedFrom":sQuery(id+"F0.wireOp",EDGE,"E78")}),-1.0]])]});
            extrude(context, id + "F3", {"entities" : qUnion([Q0]), "operationType" : NewBodyOperationType.ADD, "depth" : 3.17 * mm});
        }
    });
